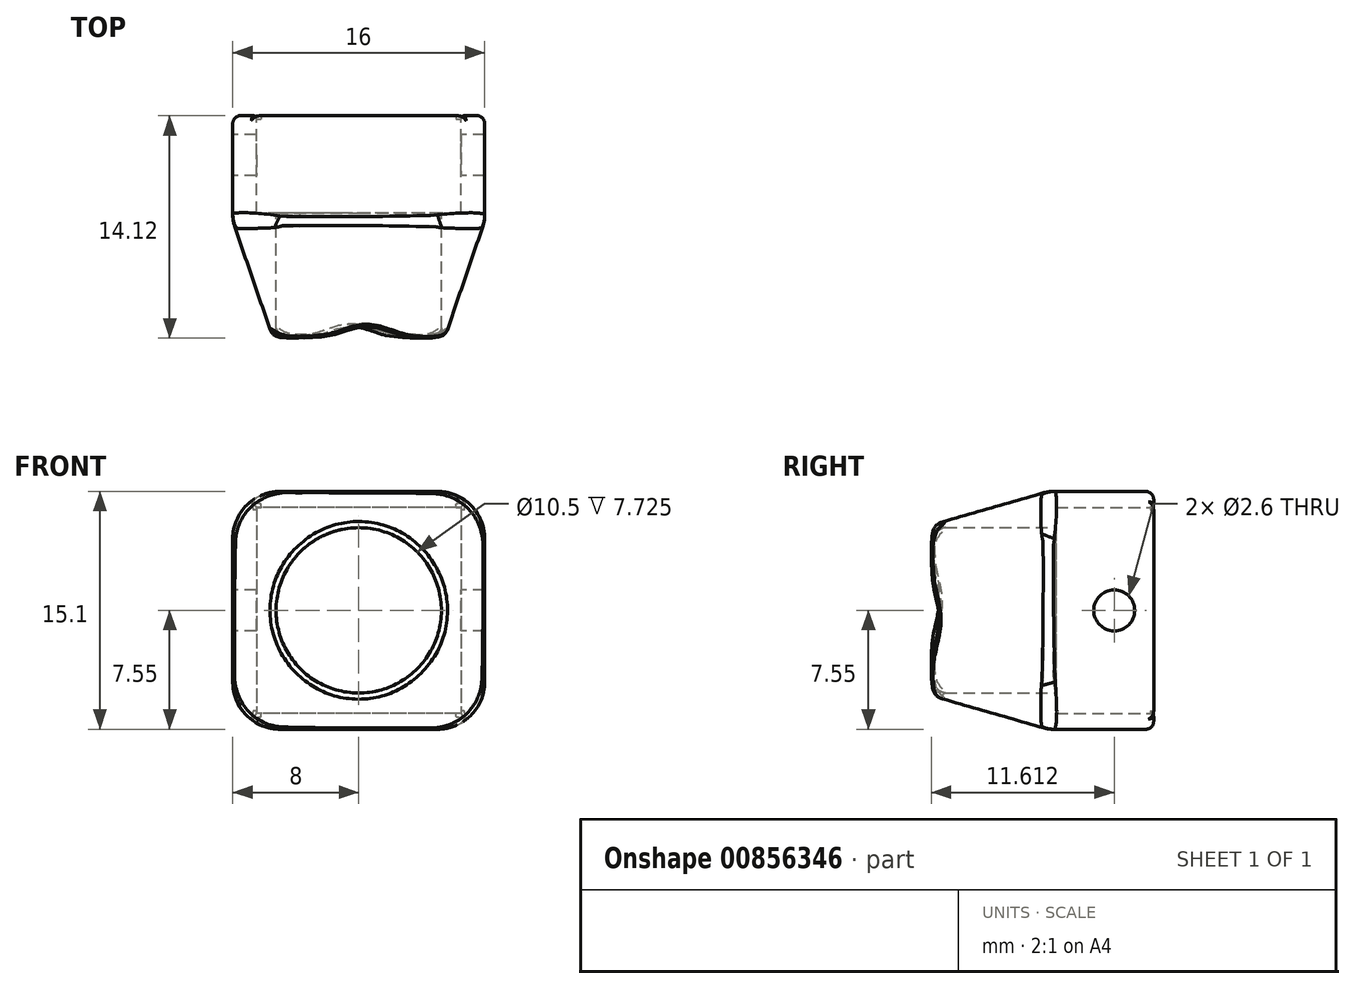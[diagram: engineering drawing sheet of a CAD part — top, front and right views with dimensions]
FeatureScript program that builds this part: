
annotation { "Feature Type Name" : "Feature", "Feature Type Description" : "" }
export const myFeature = defineFeature(function(context is Context, id is Id, definition is map)
    precondition{}
    {
        {
            var Q0;
            Q0=qCreatedBy(makeId("Front.planeOp"),FACE);
            var sketch = newSketch(context, id + "F0", { "sketchPlane" : qUnion([Q0])});
            skLineSegment(sketch, "E0.bottom", {"start": v(6.5, 6.55) * mm, "end": v(-6.5, 6.55) * mm});
            skLineSegment(sketch, "E0.top", {"start": v(6.5, -6.55) * mm, "end": v(-6.5, -6.55) * mm});
            skLineSegment(sketch, "E0.left", {"start": v(6.5, 6.55) * mm, "end": v(6.5, -6.55) * mm});
            skLineSegment(sketch, "E0.right", {"start": v(-6.5, 6.55) * mm, "end": v(-6.5, -6.55) * mm});
            skPoint(sketch, "E0.middle", {"position": v(0, 0) * mm});
            skLineSegment(sketch, "E1.bottom", {"start": v(8, 7.55) * mm, "end": v(-8, 7.55) * mm});
            skLineSegment(sketch, "E1.top", {"start": v(8, -7.55) * mm, "end": v(-8, -7.55) * mm});
            skLineSegment(sketch, "E1.left", {"start": v(8, 7.55) * mm, "end": v(8, -7.55) * mm});
            skLineSegment(sketch, "E1.right", {"start": v(-8, 7.55) * mm, "end": v(-8, -7.55) * mm});
            skSolve(sketch);
        }
        {
            var Q0;
            Q0 = qSketchRegion(id + "F0", true);
            extrude(context, id + "F1", {"entities" : qUnion([Q0]), "depth" : 6.2 * mm, "offsetDistance" : 25 * mm});
        }
        {
            var Q0;
            Q0=makeQuery(id+"F1.opExtrude","CAP_FACE",FACE,{"disambiguationData":[OSD([sQuery(id+"F0.wireOp",EDGE,"E0.bottom"),sQuery(id+"F0.wireOp",EDGE,"E0.top"),sQuery(id+"F0.wireOp",EDGE,"E0.left"),sQuery(id+"F0.wireOp",EDGE,"E0.right"),sQuery(id+"F0.wireOp",EDGE,"E1.bottom"),sQuery(id+"F0.wireOp",EDGE,"E1.top"),sQuery(id+"F0.wireOp",EDGE,"E1.left"),sQuery(id+"F0.wireOp",EDGE,"E1.right")])],"isStart":false});
            var sketch = newSketch(context, id + "F2", { "sketchPlane" : qUnion([Q0])});
            skLineSegment(sketch, "E2.bottom", {"start": v(-8, 7.55) * mm, "end": v(8, 7.55) * mm});
            skLineSegment(sketch, "E2.top", {"start": v(-8, -7.55) * mm, "end": v(8, -7.55) * mm});
            skLineSegment(sketch, "E2.left", {"start": v(-8, 7.55) * mm, "end": v(-8, -7.55) * mm});
            skLineSegment(sketch, "E2.right", {"start": v(8, 7.55) * mm, "end": v(8, -7.55) * mm});
            skCircle(sketch, "E3", {"center": v(0, 0) * mm, "radius": 5.25 * mm});
            skSolve(sketch);
        }
        {
            var Q0;
            Q0 = qSketchRegion(id + "F2", true);
            extrude(context, id + "F3", {"entities" : qUnion([Q0]), "operationType" : NewBodyOperationType.ADD, "depth" : .5 * mm, "offsetDistance" : 25 * mm});
        }
        {
            var Q0;
            Q0=makeQuery(id+"F3.boolean.opBoolean","MERGE",FACE,{"derivedFrom":[makeQuery(id+"F1.opExtrude","SWEPT_FACE",FACE,{"disambiguationData":[OSD([sQuery(id+"F0.wireOp",EDGE,"E1.right")])]}),makeQuery(id+"F3.opExtrude","SWEPT_FACE",FACE,{"disambiguationData":[OSD([sQuery(id+"F2.wireOp",EDGE,"E2.left")])]})]});
            var sketch = newSketch(context, id + "F4", { "sketchPlane" : qUnion([Q0])});
            skCircle(sketch, "E4", {"center": v(2.5, 0) * mm, "radius": 1.3 * mm});
            skSolve(sketch);
        }
        {
            var Q0;
            Q0 = qSketchRegion(id + "F4", true);
            extrude(context, id + "F5", {"entities" : qUnion([Q0]), "operationType" : NewBodyOperationType.REMOVE, "oppositeDirection" : true, "depth" : 25 * mm, "offsetDistance" : 25 * mm});
        }
        {
            var Q0;
            Q0=makeQuery(id+"F3.boolean.opBoolean","MERGE",EDGE,{"derivedFrom":[makeQuery(id+"F1.opExtrude","SWEPT_EDGE",EDGE,{"disambiguationData":[OSD([sQuery(id+"F0.wireOp",EDGE,"E1.bottom"),sQuery(id+"F0.wireOp",EDGE,"E1.left")])]}),makeQuery(id+"F3.opExtrude","SWEPT_EDGE",EDGE,{"disambiguationData":[OSD([sQuery(id+"F2.wireOp",EDGE,"E2.bottom"),sQuery(id+"F2.wireOp",EDGE,"E2.right")])]})]});
            var Q1;
            Q1=makeQuery(id+"F3.boolean.opBoolean","MERGE",EDGE,{"derivedFrom":[makeQuery(id+"F1.opExtrude","SWEPT_EDGE",EDGE,{"disambiguationData":[OSD([sQuery(id+"F0.wireOp",EDGE,"E1.top"),sQuery(id+"F0.wireOp",EDGE,"E1.left")])]}),makeQuery(id+"F3.opExtrude","SWEPT_EDGE",EDGE,{"disambiguationData":[OSD([sQuery(id+"F2.wireOp",EDGE,"E2.top"),sQuery(id+"F2.wireOp",EDGE,"E2.right")])]})]});
            var Q2;
            Q2=makeQuery(id+"F3.boolean.opBoolean","MERGE",EDGE,{"derivedFrom":[makeQuery(id+"F1.opExtrude","SWEPT_EDGE",EDGE,{"disambiguationData":[OSD([sQuery(id+"F0.wireOp",EDGE,"E1.top"),sQuery(id+"F0.wireOp",EDGE,"E1.right")])]}),makeQuery(id+"F3.opExtrude","SWEPT_EDGE",EDGE,{"disambiguationData":[OSD([sQuery(id+"F2.wireOp",EDGE,"E2.top"),sQuery(id+"F2.wireOp",EDGE,"E2.left")])]})]});
            var Q3;
            Q3=makeQuery(id+"F3.boolean.opBoolean","MERGE",EDGE,{"derivedFrom":[makeQuery(id+"F1.opExtrude","SWEPT_EDGE",EDGE,{"disambiguationData":[OSD([sQuery(id+"F0.wireOp",EDGE,"E1.bottom"),sQuery(id+"F0.wireOp",EDGE,"E1.right")])]}),makeQuery(id+"F3.opExtrude","SWEPT_EDGE",EDGE,{"disambiguationData":[OSD([sQuery(id+"F2.wireOp",EDGE,"E2.bottom"),sQuery(id+"F2.wireOp",EDGE,"E2.left")])]})]});
            fillet(context, id + "F6", {"entities" : qUnion([Q0, Q1, Q2, Q3]), "radius" : 3 * mm, "tangentPropagation" : true, "allowEdgeOverflow" : false});
        }
        {
            var Q0;
            Q0=makeQuery(id+"F1.opExtrude","CAP_EDGE",EDGE,{"disambiguationData":[OSD([sQuery(id+"F0.wireOp",EDGE,"E1.right")])],"isStart":true});
            var Q1;
            Q1=makeQuery(id+"F1.opExtrude","CAP_EDGE",EDGE,{"disambiguationData":[OSD([sQuery(id+"F0.wireOp",EDGE,"E1.bottom")])],"isStart":true});
            var Q2;
            {var subQ0=sQuery(id+"F0.wireOp",EDGE,"E1.right");var subQ1=sQuery(id+"F0.wireOp",EDGE,"E1.bottom");Q2=makeQuery(id+"F6.opFillet","BLEND_EDGE",EDGE,{"blendedFrom":[makeQuery(id+"F3.boolean.opBoolean","MERGE",EDGE,{"derivedFrom":[makeQuery(id+"F1.opExtrude","SWEPT_EDGE",EDGE,{"disambiguationData":[OSD([subQ1,subQ0])]}),makeQuery(id+"F3.opExtrude","SWEPT_EDGE",EDGE,{"disambiguationData":[OSD([sQuery(id+"F2.wireOp",EDGE,"E2.bottom"),sQuery(id+"F2.wireOp",EDGE,"E2.left")])]})]}),makeQuery(id+"F1.opExtrude","CAP_FACE",FACE,{"disambiguationData":[OSD([sQuery(id+"F0.wireOp",EDGE,"E0.bottom"),sQuery(id+"F0.wireOp",EDGE,"E0.top"),sQuery(id+"F0.wireOp",EDGE,"E0.left"),sQuery(id+"F0.wireOp",EDGE,"E0.right"),subQ1,sQuery(id+"F0.wireOp",EDGE,"E1.top"),sQuery(id+"F0.wireOp",EDGE,"E1.left"),subQ0])],"isStart":true})],"blendedInto":[makeQuery(id+"F1.opExtrude","CAP_FACE",FACE,{"disambiguationData":[OSD([sQuery(id+"F0.wireOp",EDGE,"E0.bottom"),sQuery(id+"F0.wireOp",EDGE,"E0.top"),sQuery(id+"F0.wireOp",EDGE,"E0.left"),sQuery(id+"F0.wireOp",EDGE,"E0.right"),subQ1,sQuery(id+"F0.wireOp",EDGE,"E1.top"),sQuery(id+"F0.wireOp",EDGE,"E1.left"),subQ0])],"isStart":true})]});}
            var Q3;
            {var subQ0=sQuery(id+"F0.wireOp",EDGE,"E1.right");var subQ1=sQuery(id+"F0.wireOp",EDGE,"E1.top");Q3=makeQuery(id+"F6.opFillet","BLEND_EDGE",EDGE,{"blendedFrom":[makeQuery(id+"F3.boolean.opBoolean","MERGE",EDGE,{"derivedFrom":[makeQuery(id+"F1.opExtrude","SWEPT_EDGE",EDGE,{"disambiguationData":[OSD([subQ1,subQ0])]}),makeQuery(id+"F3.opExtrude","SWEPT_EDGE",EDGE,{"disambiguationData":[OSD([sQuery(id+"F2.wireOp",EDGE,"E2.top"),sQuery(id+"F2.wireOp",EDGE,"E2.left")])]})]}),makeQuery(id+"F1.opExtrude","CAP_FACE",FACE,{"disambiguationData":[OSD([sQuery(id+"F0.wireOp",EDGE,"E0.bottom"),sQuery(id+"F0.wireOp",EDGE,"E0.top"),sQuery(id+"F0.wireOp",EDGE,"E0.left"),sQuery(id+"F0.wireOp",EDGE,"E0.right"),sQuery(id+"F0.wireOp",EDGE,"E1.bottom"),subQ1,sQuery(id+"F0.wireOp",EDGE,"E1.left"),subQ0])],"isStart":true})],"blendedInto":[makeQuery(id+"F1.opExtrude","CAP_FACE",FACE,{"disambiguationData":[OSD([sQuery(id+"F0.wireOp",EDGE,"E0.bottom"),sQuery(id+"F0.wireOp",EDGE,"E0.top"),sQuery(id+"F0.wireOp",EDGE,"E0.left"),sQuery(id+"F0.wireOp",EDGE,"E0.right"),sQuery(id+"F0.wireOp",EDGE,"E1.bottom"),subQ1,sQuery(id+"F0.wireOp",EDGE,"E1.left"),subQ0])],"isStart":true})]});}
            var Q4;
            Q4=makeQuery(id+"F1.opExtrude","CAP_EDGE",EDGE,{"disambiguationData":[OSD([sQuery(id+"F0.wireOp",EDGE,"E1.top")])],"isStart":true});
            var Q5;
            {var subQ0=sQuery(id+"F0.wireOp",EDGE,"E1.left");var subQ1=sQuery(id+"F0.wireOp",EDGE,"E1.bottom");Q5=makeQuery(id+"F6.opFillet","BLEND_EDGE",EDGE,{"blendedFrom":[makeQuery(id+"F3.boolean.opBoolean","MERGE",EDGE,{"derivedFrom":[makeQuery(id+"F1.opExtrude","SWEPT_EDGE",EDGE,{"disambiguationData":[OSD([subQ1,subQ0])]}),makeQuery(id+"F3.opExtrude","SWEPT_EDGE",EDGE,{"disambiguationData":[OSD([sQuery(id+"F2.wireOp",EDGE,"E2.bottom"),sQuery(id+"F2.wireOp",EDGE,"E2.right")])]})]}),makeQuery(id+"F1.opExtrude","CAP_FACE",FACE,{"disambiguationData":[OSD([sQuery(id+"F0.wireOp",EDGE,"E0.bottom"),sQuery(id+"F0.wireOp",EDGE,"E0.top"),sQuery(id+"F0.wireOp",EDGE,"E0.left"),sQuery(id+"F0.wireOp",EDGE,"E0.right"),subQ1,sQuery(id+"F0.wireOp",EDGE,"E1.top"),subQ0,sQuery(id+"F0.wireOp",EDGE,"E1.right")])],"isStart":true})],"blendedInto":[makeQuery(id+"F1.opExtrude","CAP_FACE",FACE,{"disambiguationData":[OSD([sQuery(id+"F0.wireOp",EDGE,"E0.bottom"),sQuery(id+"F0.wireOp",EDGE,"E0.top"),sQuery(id+"F0.wireOp",EDGE,"E0.left"),sQuery(id+"F0.wireOp",EDGE,"E0.right"),subQ1,sQuery(id+"F0.wireOp",EDGE,"E1.top"),subQ0,sQuery(id+"F0.wireOp",EDGE,"E1.right")])],"isStart":true})]});}
            var Q6;
            {var subQ0=sQuery(id+"F0.wireOp",EDGE,"E1.left");var subQ1=sQuery(id+"F0.wireOp",EDGE,"E1.top");Q6=makeQuery(id+"F6.opFillet","BLEND_EDGE",EDGE,{"blendedFrom":[makeQuery(id+"F3.boolean.opBoolean","MERGE",EDGE,{"derivedFrom":[makeQuery(id+"F1.opExtrude","SWEPT_EDGE",EDGE,{"disambiguationData":[OSD([subQ1,subQ0])]}),makeQuery(id+"F3.opExtrude","SWEPT_EDGE",EDGE,{"disambiguationData":[OSD([sQuery(id+"F2.wireOp",EDGE,"E2.top"),sQuery(id+"F2.wireOp",EDGE,"E2.right")])]})]}),makeQuery(id+"F1.opExtrude","CAP_FACE",FACE,{"disambiguationData":[OSD([sQuery(id+"F0.wireOp",EDGE,"E0.bottom"),sQuery(id+"F0.wireOp",EDGE,"E0.top"),sQuery(id+"F0.wireOp",EDGE,"E0.left"),sQuery(id+"F0.wireOp",EDGE,"E0.right"),sQuery(id+"F0.wireOp",EDGE,"E1.bottom"),subQ1,subQ0,sQuery(id+"F0.wireOp",EDGE,"E1.right")])],"isStart":true})],"blendedInto":[makeQuery(id+"F1.opExtrude","CAP_FACE",FACE,{"disambiguationData":[OSD([sQuery(id+"F0.wireOp",EDGE,"E0.bottom"),sQuery(id+"F0.wireOp",EDGE,"E0.top"),sQuery(id+"F0.wireOp",EDGE,"E0.left"),sQuery(id+"F0.wireOp",EDGE,"E0.right"),sQuery(id+"F0.wireOp",EDGE,"E1.bottom"),subQ1,subQ0,sQuery(id+"F0.wireOp",EDGE,"E1.right")])],"isStart":true})]});}
            fillet(context, id + "F7", {"entities" : qUnion([Q0, Q1, Q2, Q3, Q4, Q5, Q6]), "radius" : .5 * mm, "tangentPropagation" : true, "allowEdgeOverflow" : false});
        }
        {
            var Q0;
            Q0=makeQuery(id+"F1.opExtrude","CAP_EDGE",EDGE,{"disambiguationData":[OSD([sQuery(id+"F0.wireOp",EDGE,"E0.left")])],"isStart":true});
            var Q1;
            Q1=makeQuery(id+"F7.opFillet","BLEND_EDGE",EDGE,{"blendedFrom":[makeQuery(id+"F1.opExtrude","CAP_EDGE",EDGE,{"disambiguationData":[OSD([sQuery(id+"F0.wireOp",EDGE,"E1.bottom")])],"isStart":true}),makeQuery(id+"F1.opExtrude","SWEPT_FACE",FACE,{"disambiguationData":[OSD([sQuery(id+"F0.wireOp",EDGE,"E0.bottom")])]})],"blendedInto":[makeQuery(id+"F1.opExtrude","SWEPT_FACE",FACE,{"disambiguationData":[OSD([sQuery(id+"F0.wireOp",EDGE,"E0.bottom")])]})]});
            var Q2;
            Q2=makeQuery(id+"F1.opExtrude","CAP_EDGE",EDGE,{"disambiguationData":[OSD([sQuery(id+"F0.wireOp",EDGE,"E0.right")])],"isStart":true});
            var Q3;
            Q3=makeQuery(id+"F7.opFillet","BLEND_EDGE",EDGE,{"blendedFrom":[makeQuery(id+"F1.opExtrude","CAP_EDGE",EDGE,{"disambiguationData":[OSD([sQuery(id+"F0.wireOp",EDGE,"E1.top")])],"isStart":true}),makeQuery(id+"F1.opExtrude","SWEPT_FACE",FACE,{"disambiguationData":[OSD([sQuery(id+"F0.wireOp",EDGE,"E0.top")])]})],"blendedInto":[makeQuery(id+"F1.opExtrude","SWEPT_FACE",FACE,{"disambiguationData":[OSD([sQuery(id+"F0.wireOp",EDGE,"E0.top")])]})]});
            var Q4;
            Q4=makeQuery(id+"F1.opExtrude","CAP_EDGE",EDGE,{"disambiguationData":[OSD([sQuery(id+"F0.wireOp",EDGE,"E0.top")])],"isStart":true});
            var Q5;
            Q5=makeQuery(id+"F1.opExtrude","CAP_EDGE",EDGE,{"disambiguationData":[OSD([sQuery(id+"F0.wireOp",EDGE,"E0.bottom")])],"isStart":true});
            fillet(context, id + "F8", {"entities" : qUnion([Q0, Q1, Q2, Q3, Q4, Q5]), "radius" : .2 * mm, "tangentPropagation" : true, "allowEdgeOverflow" : false});
        }
        {
            var Q0;
            Q0=makeQuery(id+"F3.opExtrude","CAP_FACE",FACE,{"disambiguationData":[OSD([sQuery(id+"F2.wireOp",EDGE,"E2.bottom"),sQuery(id+"F2.wireOp",EDGE,"E2.top"),sQuery(id+"F2.wireOp",EDGE,"E2.left"),sQuery(id+"F2.wireOp",EDGE,"E2.right"),sQuery(id+"F2.wireOp",EDGE,"E3")])],"isStart":false});
            var sketch = newSketch(context, id + "F9", { "sketchPlane" : qUnion([Q0])});
            skLineSegment(sketch, "E5.0", {"start": v(5, 7.55) * mm, "end": v(-5, 7.55) * mm});
            skArc(sketch, "E6.0", {"start": v(8, 4.55) * mm, "mid": v(7.12, 6.67) * mm, "end": v(5, 7.55) * mm});
            skLineSegment(sketch, "E7.0", {"start": v(8, 4.55) * mm, "end": v(8, -4.55) * mm});
            skArc(sketch, "E8.0", {"start": v(5, -7.55) * mm, "mid": v(7.12, -6.67) * mm, "end": v(8, -4.55) * mm});
            skLineSegment(sketch, "E9.0", {"start": v(5, -7.55) * mm, "end": v(-5, -7.55) * mm});
            skArc(sketch, "E10.0", {"start": v(-8, -4.55) * mm, "mid": v(-7.12, -6.67) * mm, "end": v(-5, -7.55) * mm});
            skLineSegment(sketch, "E11.0", {"start": v(-8, 4.55) * mm, "end": v(-8, -4.55) * mm});
            skArc(sketch, "E12.0", {"start": v(-5, 7.55) * mm, "mid": v(-7.12, 6.67) * mm, "end": v(-8, 4.55) * mm});
            skSolve(sketch);
        }
        {
            var Q0;
            Q0=makeQuery(id+"F9.imprint","IMPRINT",FACE,{"disambiguationData":[TD([[makeQuery(id+"F9.imprint","IMPRINT",EDGE,{"derivedFrom":sQuery(id+"F9.wireOp",EDGE,"E5.0")}),1.0]])]});
            cPlane(context, id + "F10", {"entities" : qUnion([Q0]), "cplaneType" : CPlaneType.OFFSET, "offset" : 8 * mm, "width" : 150 * mm, "height" : 150 * mm});
        }
        {
            var Q0;
            Q0=qCreatedBy(id+"F10.planeOp",FACE);
            var sketch = newSketch(context, id + "F11", { "sketchPlane" : qUnion([Q0])});
            skCircle(sketch, "E13.0", {"center": v(0, 0) * mm, "radius": 5.25 * mm});
            skSolve(sketch);
        }
        {
            var Q1;
            Q1 = qSketchRegion(id + "F9", true);
            var Q2;
            Q2 = qSketchRegion(id + "F11", true);
            loft(context, id + "F12", {"operationType" : NewBodyOperationType.ADD, "sheetProfilesArray" : [{ "sheetProfileEntities" : qUnion([Q1]) }, { "sheetProfileEntities" : qUnion([Q2]) }]});
        }
        {
            var Q0;
            Q0=makeQuery(id+"F12.opLoft","CAP_FACE",FACE,{"disambiguationData":[OSD([makeQuery(id+"F9.imprint","IMPRINT",FACE,{"disambiguationData":[TD([[makeQuery(id+"F9.imprint","IMPRINT",EDGE,{"derivedFrom":makeQuery(id+"F3.opExtrude","CAP_EDGE",EDGE,{"disambiguationData":[OSD([sQuery(id+"F2.wireOp",EDGE,"E3")])],"isStart":false})}),1.0]])]})])],"isStart":true});
            extrude(context, id + "F13", {"entities" : qUnion([Q0]), "operationType" : NewBodyOperationType.REMOVE, "oppositeDirection" : true, "depth" : 25 * mm, "offsetDistance" : 25 * mm});
        }
        {
            var Q0;
            Q0=makeQuery(id+"F12.opLoft","MID_CAP_EDGE",EDGE,{"disambiguationData":[OSD([sQuery(id+"F9.wireOp",EDGE,"E10.0"),sQuery(id+"F9.wireOp",EDGE,"E11.0"),sQuery(id+"F9.wireOp",EDGE,"E12.0"),sQuery(id+"F11.wireOp",EDGE,"E13.0")])],"capPos":1.0});
            var Q1;
            Q1=makeQuery(id+"F12.opLoft","MID_CAP_EDGE",EDGE,{"disambiguationData":[OSD([sQuery(id+"F9.wireOp",EDGE,"E5.0"),sQuery(id+"F9.wireOp",EDGE,"E11.0"),sQuery(id+"F9.wireOp",EDGE,"E12.0"),sQuery(id+"F11.wireOp",EDGE,"E13.0")])],"capPos":1.0});
            var Q2;
            Q2=makeQuery(id+"F12.opLoft","MID_CAP_EDGE",EDGE,{"disambiguationData":[OSD([sQuery(id+"F9.wireOp",EDGE,"E5.0"),sQuery(id+"F9.wireOp",EDGE,"E6.0"),sQuery(id+"F9.wireOp",EDGE,"E12.0"),sQuery(id+"F11.wireOp",EDGE,"E13.0")])],"capPos":1.0});
            var Q3;
            Q3=makeQuery(id+"F12.opLoft","MID_CAP_EDGE",EDGE,{"disambiguationData":[OSD([sQuery(id+"F9.wireOp",EDGE,"E5.0"),sQuery(id+"F9.wireOp",EDGE,"E6.0"),sQuery(id+"F11.wireOp",EDGE,"E13.0")])],"capPos":1.0});
            var Q4;
            Q4=makeQuery(id+"F12.opLoft","MID_CAP_EDGE",EDGE,{"disambiguationData":[OSD([sQuery(id+"F9.wireOp",EDGE,"E5.0"),sQuery(id+"F9.wireOp",EDGE,"E6.0"),sQuery(id+"F9.wireOp",EDGE,"E7.0"),sQuery(id+"F9.wireOp",EDGE,"E8.0"),sQuery(id+"F11.wireOp",EDGE,"E13.0")])],"capPos":1.0});
            var Q5;
            Q5=makeQuery(id+"F12.opLoft","MID_CAP_EDGE",EDGE,{"disambiguationData":[OSD([sQuery(id+"F9.wireOp",EDGE,"E7.0"),sQuery(id+"F9.wireOp",EDGE,"E8.0"),sQuery(id+"F9.wireOp",EDGE,"E9.0"),sQuery(id+"F11.wireOp",EDGE,"E13.0")])],"capPos":1.0});
            var Q6;
            Q6=makeQuery(id+"F12.opLoft","MID_CAP_EDGE",EDGE,{"disambiguationData":[OSD([sQuery(id+"F9.wireOp",EDGE,"E8.0"),sQuery(id+"F9.wireOp",EDGE,"E9.0"),sQuery(id+"F9.wireOp",EDGE,"E10.0"),sQuery(id+"F11.wireOp",EDGE,"E13.0")])],"capPos":1.0});
            var Q7;
            Q7=makeQuery(id+"F12.opLoft","MID_CAP_EDGE",EDGE,{"disambiguationData":[OSD([sQuery(id+"F9.wireOp",EDGE,"E9.0"),sQuery(id+"F9.wireOp",EDGE,"E10.0"),sQuery(id+"F9.wireOp",EDGE,"E11.0"),sQuery(id+"F11.wireOp",EDGE,"E13.0")])],"capPos":1.0});
            fillet(context, id + "F14", {"entities" : qUnion([Q0, Q1, Q2, Q3, Q4, Q5, Q6, Q7]), "radius" : .2 * mm, "tangentPropagation" : true, "allowEdgeOverflow" : false});
        }
        {
            var Q0;
            Q0=makeQuery(id+"F12.boolean.opBoolean","MERGE",EDGE,{"derivedFrom":[makeQuery(id+"F3.opExtrude","CAP_EDGE",EDGE,{"disambiguationData":[OSD([sQuery(id+"F2.wireOp",EDGE,"E2.bottom")])],"isStart":false}),makeQuery(id+"F12.opLoft","MID_CAP_EDGE",EDGE,{"disambiguationData":[OSD([sQuery(id+"F9.wireOp",EDGE,"E5.0"),sQuery(id+"F9.wireOp",EDGE,"E6.0"),sQuery(id+"F9.wireOp",EDGE,"E12.0")])],"capPos":0.0})]});
            var Q1;
            Q1=makeQuery(id+"F12.boolean.opBoolean","MERGE",EDGE,{"derivedFrom":[makeQuery(id+"F3.opExtrude","CAP_EDGE",EDGE,{"disambiguationData":[OSD([sQuery(id+"F2.wireOp",EDGE,"E2.left")])],"isStart":false}),makeQuery(id+"F12.opLoft","MID_CAP_EDGE",EDGE,{"disambiguationData":[OSD([sQuery(id+"F9.wireOp",EDGE,"E10.0"),sQuery(id+"F9.wireOp",EDGE,"E11.0"),sQuery(id+"F9.wireOp",EDGE,"E12.0")])],"capPos":0.0})]});
            var Q2;
            Q2=makeQuery(id+"F12.boolean.opBoolean","MERGE",EDGE,{"derivedFrom":[makeQuery(id+"F3.opExtrude","CAP_EDGE",EDGE,{"disambiguationData":[OSD([sQuery(id+"F2.wireOp",EDGE,"E2.top")])],"isStart":false}),makeQuery(id+"F12.opLoft","MID_CAP_EDGE",EDGE,{"disambiguationData":[OSD([sQuery(id+"F9.wireOp",EDGE,"E8.0"),sQuery(id+"F9.wireOp",EDGE,"E9.0"),sQuery(id+"F9.wireOp",EDGE,"E10.0")])],"capPos":0.0})]});
            var Q3;
            Q3=makeQuery(id+"F12.boolean.opBoolean","MERGE",EDGE,{"derivedFrom":[makeQuery(id+"F3.opExtrude","CAP_EDGE",EDGE,{"disambiguationData":[OSD([sQuery(id+"F2.wireOp",EDGE,"E2.right")])],"isStart":false}),makeQuery(id+"F12.opLoft","MID_CAP_EDGE",EDGE,{"disambiguationData":[OSD([sQuery(id+"F9.wireOp",EDGE,"E6.0"),sQuery(id+"F9.wireOp",EDGE,"E7.0"),sQuery(id+"F9.wireOp",EDGE,"E8.0")])],"capPos":0.0})]});
            fillet(context, id + "F15", {"entities" : qUnion([Q0, Q1, Q2, Q3]), "radius" : 2 * mm, "tangentPropagation" : true, "allowEdgeOverflow" : false});
        }
    });
